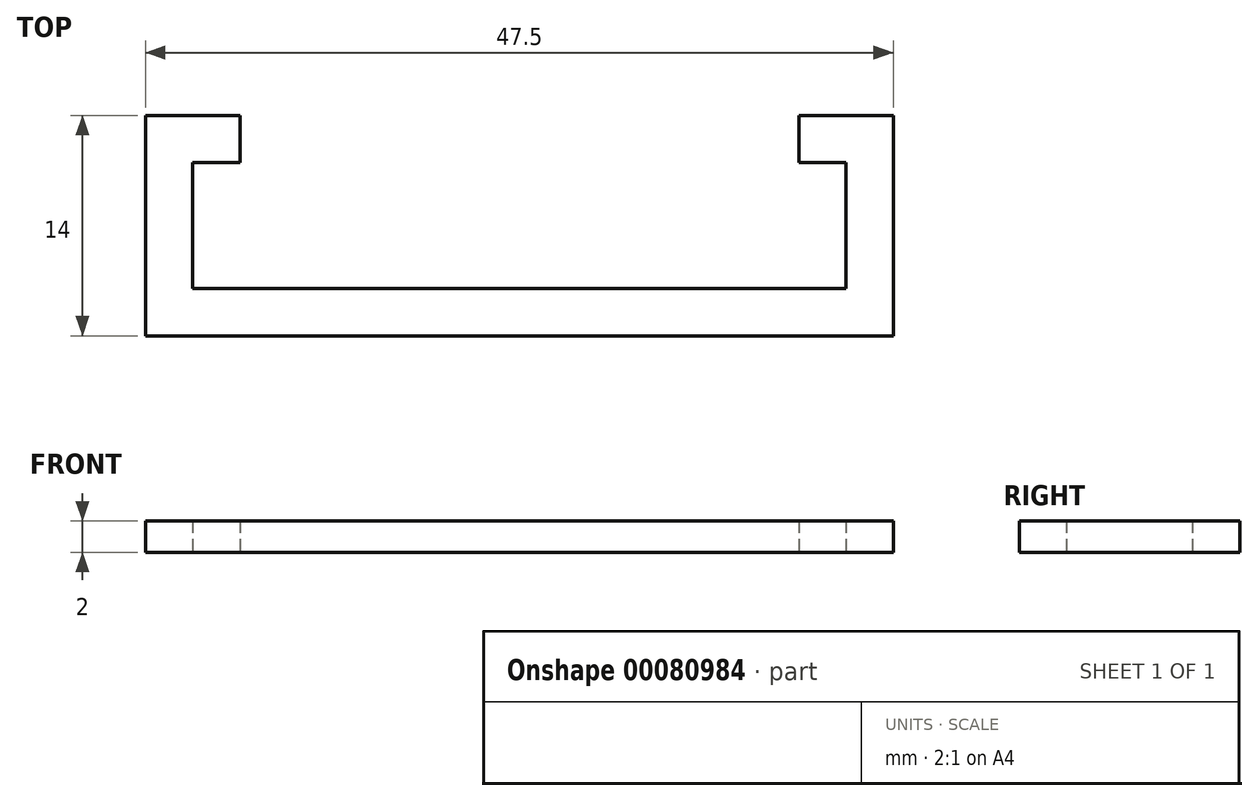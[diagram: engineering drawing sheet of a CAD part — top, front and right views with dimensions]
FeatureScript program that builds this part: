
annotation { "Feature Type Name" : "Feature", "Feature Type Description" : "" }
export const myFeature = defineFeature(function(context is Context, id is Id, definition is map)
    precondition{}
    {
        {
            var Q0;
            Q0=qCreatedBy(makeId("Top.planeOp"),FACE);
            var sketch = newSketch(context, id + "F0", { "sketchPlane" : qUnion([Q0])});
            skLineSegment(sketch, "E0.bottom", {"start": v(-20.45, 0) * mm, "end": v(27.05, 0) * mm});
            skLineSegment(sketch, "E0.top", {"start": v(-20.45, -3) * mm, "end": v(27.05, -3) * mm});
            skLineSegment(sketch, "E0.left", {"start": v(-20.45, 0) * mm, "end": v(-20.45, -3) * mm});
            skLineSegment(sketch, "E0.right", {"start": v(27.05, 0) * mm, "end": v(27.05, -3) * mm});
            skLineSegment(sketch, "E1.bottom", {"start": v(-20.45, -3) * mm, "end": v(-17.45, -3) * mm});
            skLineSegment(sketch, "E1.top", {"start": v(-20.45, 11) * mm, "end": v(-17.45, 11) * mm});
            skLineSegment(sketch, "E1.left", {"start": v(-20.45, -3) * mm, "end": v(-20.45, 11) * mm});
            skLineSegment(sketch, "E2.bottom", {"start": v(27.05, -3) * mm, "end": v(24.05, -3) * mm});
            skLineSegment(sketch, "E2.top", {"start": v(27.05, 11) * mm, "end": v(24.05, 11) * mm});
            skLineSegment(sketch, "E2.left", {"start": v(27.05, -3) * mm, "end": v(27.05, 11) * mm});
            skLineSegment(sketch, "E2.right", {"start": v(24.05, -3) * mm, "end": v(24.05, 11) * mm});
            skLineSegment(sketch, "E3.bottom", {"start": v(27.05, 11) * mm, "end": v(21.05, 11) * mm});
            skLineSegment(sketch, "E3.top", {"start": v(27.05, 8) * mm, "end": v(21.05, 8) * mm});
            skLineSegment(sketch, "E3.left", {"start": v(27.05, 11) * mm, "end": v(27.05, 8) * mm});
            skLineSegment(sketch, "E3.right", {"start": v(21.05, 11) * mm, "end": v(21.05, 8) * mm});
            skLineSegment(sketch, "E4", {"start": v(-20.45, -3) * mm, "end": v(-20.45, 0) * mm});
            skLineSegment(sketch, "E5", {"start": v(24.05, 0) * mm, "end": v(24.05, 8) * mm});
            skLineSegment(sketch, "E6", {"start": v(-17.45, 0) * mm, "end": v(24.05, 0) * mm});
            skLineSegment(sketch, "E7", {"start": v(-17.45, -3) * mm, "end": v(24.05, -3) * mm});
            skLineSegment(sketch, "E8", {"start": v(-17.45, -3) * mm, "end": v(-17.45, 11) * mm});
            skLineSegment(sketch, "E9.bottom", {"start": v(-20.45, 11) * mm, "end": v(-14.45, 11) * mm});
            skLineSegment(sketch, "E9.top", {"start": v(-20.45, 8) * mm, "end": v(-14.45, 8) * mm});
            skLineSegment(sketch, "E9.left", {"start": v(-20.45, 11) * mm, "end": v(-20.45, 8) * mm});
            skLineSegment(sketch, "E9.right", {"start": v(-14.45, 11) * mm, "end": v(-14.45, 8) * mm});
            skLineSegment(sketch, "E10", {"start": v(-17.45, 0) * mm, "end": v(-17.45, 8) * mm});
            skLineSegment(sketch, "E11", {"start": v(-17.45, 8) * mm, "end": v(-17.45, 0) * mm});
            skSolve(sketch);
        }
        {
            var Q0;
            Q0=qSketchRegion(id+"F0",true);
            extrude(context, id + "F1", {"entities" : qUnion([Q0]), "depth" : 2 * mm});
        }
    });
